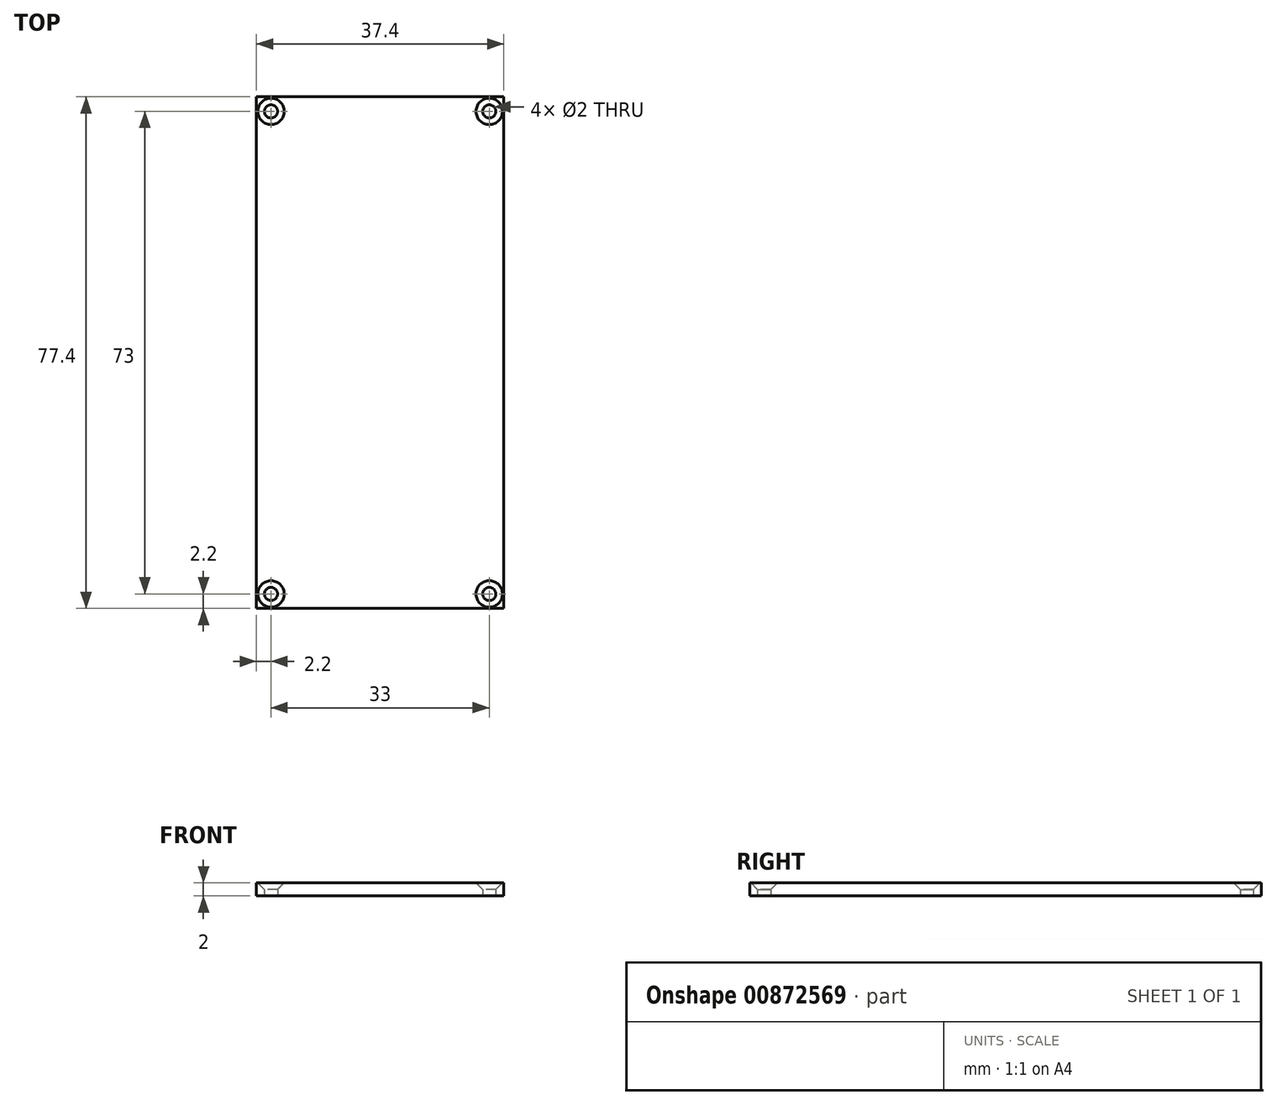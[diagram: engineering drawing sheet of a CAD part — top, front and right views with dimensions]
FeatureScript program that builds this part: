
annotation { "Feature Type Name" : "Feature", "Feature Type Description" : "" }
export const myFeature = defineFeature(function(context is Context, id is Id, definition is map)
    precondition{}
    {
        {
            var Q0;
            Q0=qCreatedBy(makeId("Top.planeOp"),FACE);
            var sketch = newSketch(context, id + "F0", { "sketchPlane" : qUnion([Q0])});
            skLineSegment(sketch, "E0.bottom", {"start": v(18.7, 38.7) * mm, "end": v(-18.7, 38.7) * mm});
            skLineSegment(sketch, "E0.top", {"start": v(18.7, -38.7) * mm, "end": v(-18.7, -38.7) * mm});
            skLineSegment(sketch, "E0.left", {"start": v(18.7, 38.7) * mm, "end": v(18.7, -38.7) * mm});
            skLineSegment(sketch, "E0.right", {"start": v(-18.7, 38.7) * mm, "end": v(-18.7, -38.7) * mm});
            skPoint(sketch, "E0.middle", {"position": v(0, 0) * mm});
            skCircle(sketch, "E1", {"center": v(-16.5, 36.5) * mm, "radius": 1 * mm});
            skCircle(sketch, "E2.0.1.0", {"center": v(-16.5, -36.5) * mm, "radius": 1 * mm});
            skCircle(sketch, "E2.1.0.0", {"center": v(16.5, 36.5) * mm, "radius": 1 * mm});
            skCircle(sketch, "E2.1.1.0", {"center": v(16.5, -36.5) * mm, "radius": 1 * mm});
            skLineSegment(sketch, "E2.direction1", {"start": v(-16.5, 36.5) * mm, "end": v(16.5, 36.5) * mm, "construction": true});
            skLineSegment(sketch, "E2.direction2", {"start": v(-16.5, 36.5) * mm, "end": v(-16.5, -36.5) * mm, "construction": true});
            skSolve(sketch);
        }
        {
            var Q0;
            Q0 = qSketchRegion(id + "F0", true);
            extrude(context, id + "F1", {"entities" : qUnion([Q0]), "depth" : 2 * mm, "offsetDistance" : 25 * mm});
        }
        {
            var Q0;
            Q0=makeQuery(id+"F1.opExtrude","CAP_EDGE",EDGE,{"disambiguationData":[OSD([sQuery(id+"F0.wireOp",EDGE,"E2.0.1.0")])],"isStart":false});
            var Q1;
            Q1=makeQuery(id+"F1.opExtrude","CAP_EDGE",EDGE,{"disambiguationData":[OSD([sQuery(id+"F0.wireOp",EDGE,"E2.1.1.0")])],"isStart":false});
            var Q2;
            Q2=makeQuery(id+"F1.opExtrude","CAP_EDGE",EDGE,{"disambiguationData":[OSD([sQuery(id+"F0.wireOp",EDGE,"E2.1.0.0")])],"isStart":false});
            var Q3;
            Q3=makeQuery(id+"F1.opExtrude","CAP_EDGE",EDGE,{"disambiguationData":[OSD([sQuery(id+"F0.wireOp",EDGE,"E1")])],"isStart":false});
            chamfer(context, id + "F2", {"entities" : qUnion([Q0, Q1, Q2, Q3]), "chamferType" : ChamferType.OFFSET_ANGLE, "width" : 1 * mm, "oppositeDirection" : false, "angle" : 45 * degree, "tangentPropagation" : true});
        }
    });
